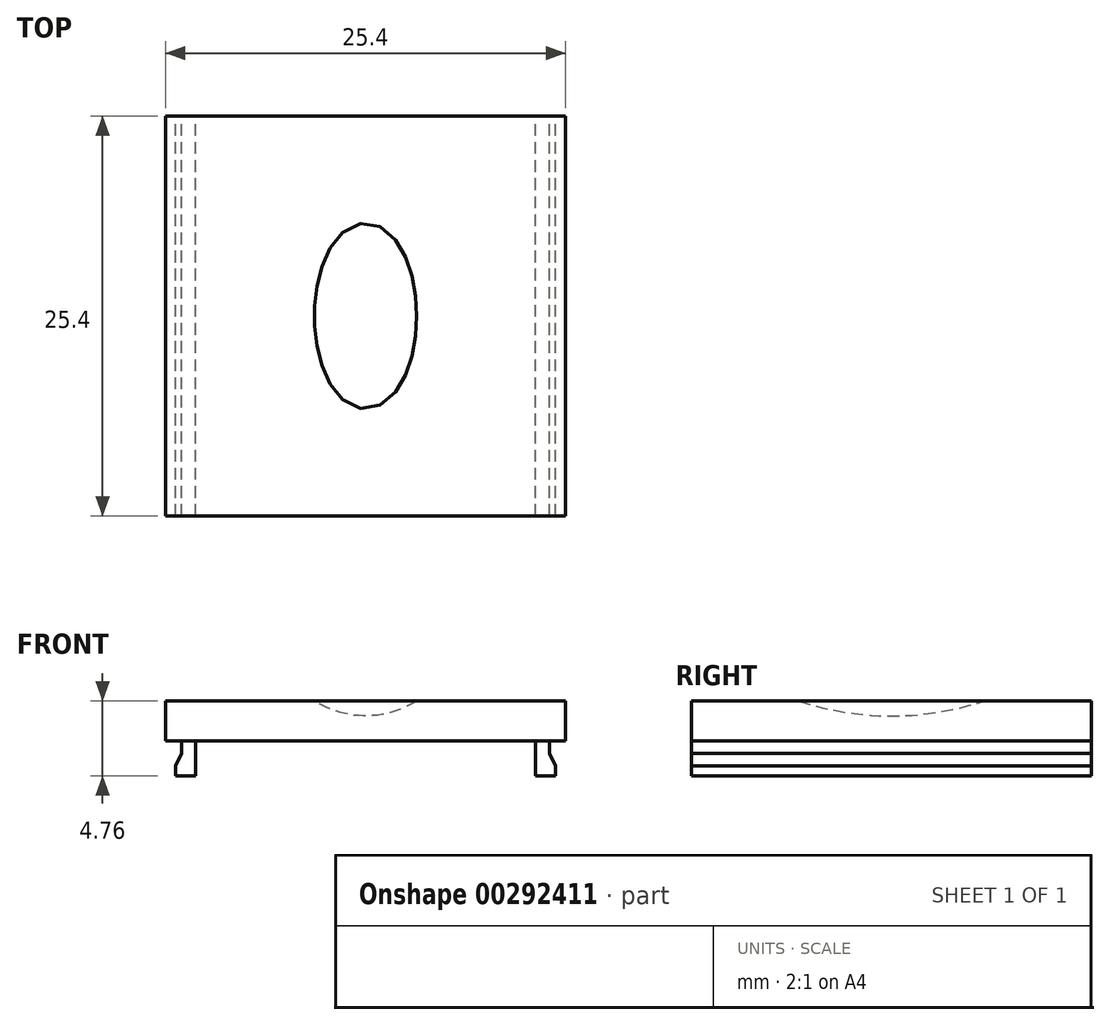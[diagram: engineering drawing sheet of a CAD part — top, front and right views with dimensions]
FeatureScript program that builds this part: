
annotation { "Feature Type Name" : "Feature", "Feature Type Description" : "" }
export const myFeature = defineFeature(function(context is Context, id is Id, definition is map)
    precondition{}
    {
        {
            var Q0;
            Q0=qCreatedBy(makeId("Top.planeOp"),FACE);
            var sketch = newSketch(context, id + "F0", { "sketchPlane" : qUnion([Q0])});
            skLineSegment(sketch, "E0.bottom", {"start": v(12.7, -12.7) * mm, "end": v(-12.7, -12.7) * mm});
            skLineSegment(sketch, "E0.top", {"start": v(12.7, 12.7) * mm, "end": v(-12.7, 12.7) * mm});
            skLineSegment(sketch, "E0.left", {"start": v(12.7, -12.7) * mm, "end": v(12.7, 12.7) * mm});
            skLineSegment(sketch, "E0.right", {"start": v(-12.7, -12.7) * mm, "end": v(-12.7, 12.7) * mm});
            skPoint(sketch, "E0.middle", {"position": v(0, 0) * mm});
            skSolve(sketch);
        }
        {
            var Q0;
            Q0=makeQuery(id+"F0.imprint","IMPRINT",FACE,{"disambiguationData":[TD([[makeQuery(id+"F0.imprint","IMPRINT",EDGE,{"derivedFrom":sQuery(id+"F0.wireOp",EDGE,"E0.bottom")}),-1.0]])]});
            extrude(context, id + "F1", {"entities" : qUnion([Q0]), "depth" : 2.54 * mm});
        }
        {
            var Q0;
            Q0=qCreatedBy(makeId("Front.planeOp"),FACE);
            var sketch = newSketch(context, id + "F2", { "sketchPlane" : qUnion([Q0])});
            skLineSegment(sketch, "E1.bottom", {"start": v(-10.8, -2.22) * mm, "end": v(-12.07, -2.22) * mm});
            skLineSegment(sketch, "E1.right", {"start": v(-12.07, -2.22) * mm, "end": v(-12.07, -1.59) * mm});
            skLineSegment(sketch, "E2.bottom", {"start": v(12.06, -2.22) * mm, "end": v(10.8, -2.22) * mm});
            skLineSegment(sketch, "E2.left", {"start": v(12.06, -2.22) * mm, "end": v(12.06, -1.59) * mm});
            skLineSegment(sketch, "E3.0", {"start": v(-11.68, 0) * mm, "end": v(-11.68, -0.8) * mm});
            skLineSegment(sketch, "E4.0", {"start": v(11.68, 0) * mm, "end": v(11.68, -0.8) * mm});
            skLineSegment(sketch, "E5", {"start": v(11.68, -0.8) * mm, "end": v(12.06, -1.59) * mm});
            skLineSegment(sketch, "E6", {"start": v(-12.07, -1.59) * mm, "end": v(-11.68, -0.8) * mm});
            skLineSegment(sketch, "E7", {"start": v(-11.68, 0) * mm, "end": v(-10.8, 0) * mm});
            skLineSegment(sketch, "E8", {"start": v(-10.8, 0) * mm, "end": v(-10.8, -2.22) * mm});
            skLineSegment(sketch, "E9", {"start": v(10.8, -2.22) * mm, "end": v(10.8, 0) * mm});
            skLineSegment(sketch, "E10", {"start": v(10.8, 0) * mm, "end": v(11.68, 0) * mm});
            skSolve(sketch);
        }
        {
            var Q0;
            Q0=makeQuery(id+"F2.imprint","IMPRINT",FACE,{"disambiguationData":[TD([[makeQuery(id+"F2.imprint","IMPRINT",EDGE,{"derivedFrom":sQuery(id+"F2.wireOp",EDGE,"E1.bottom")}),-1.0]])]});
            var Q1;
            Q1=makeQuery(id+"F2.imprint","IMPRINT",FACE,{"disambiguationData":[TD([[makeQuery(id+"F2.imprint","IMPRINT",EDGE,{"derivedFrom":sQuery(id+"F2.wireOp",EDGE,"E2.bottom")}),-1.0]])]});
            extrude(context, id + "F3", {"entities" : qUnion([Q0, Q1]), "endBound" : BoundingType.SYMMETRIC, "depth" : 25.4 * mm});
        }
        {
            var Q0;
            Q0=qCreatedBy(makeId("Front.planeOp"),FACE);
            var sketch = newSketch(context, id + "F4", { "sketchPlane" : qUnion([Q0])});
            skLineSegment(sketch, "E11", {"start": v(0, 0) * mm, "end": v(0, 2.54) * mm});
            skCircle(sketch, "E12", {"center": v(0, 7.62) * mm, "radius": 6.03 * mm});
            skLineSegment(sketch, "E13", {"start": v(0, 20.31) * mm, "end": v(7.06, 20.31) * mm});
            skSolve(sketch);
        }
        {
            var Q0;
            Q0 = qSketchRegion(id + "F4", true);
            var Q1;
            Q1=sQuery(id+"F4.wireOp",EDGE,"E13");
            revolve(context, id + "F5", {"operationType" : NewBodyOperationType.REMOVE, "entities" : qUnion([Q0]), "axis" : qUnion([Q1]), "revolveType" : RevolveType.FULL, "oppositeDirection" : true});
        }
    });
